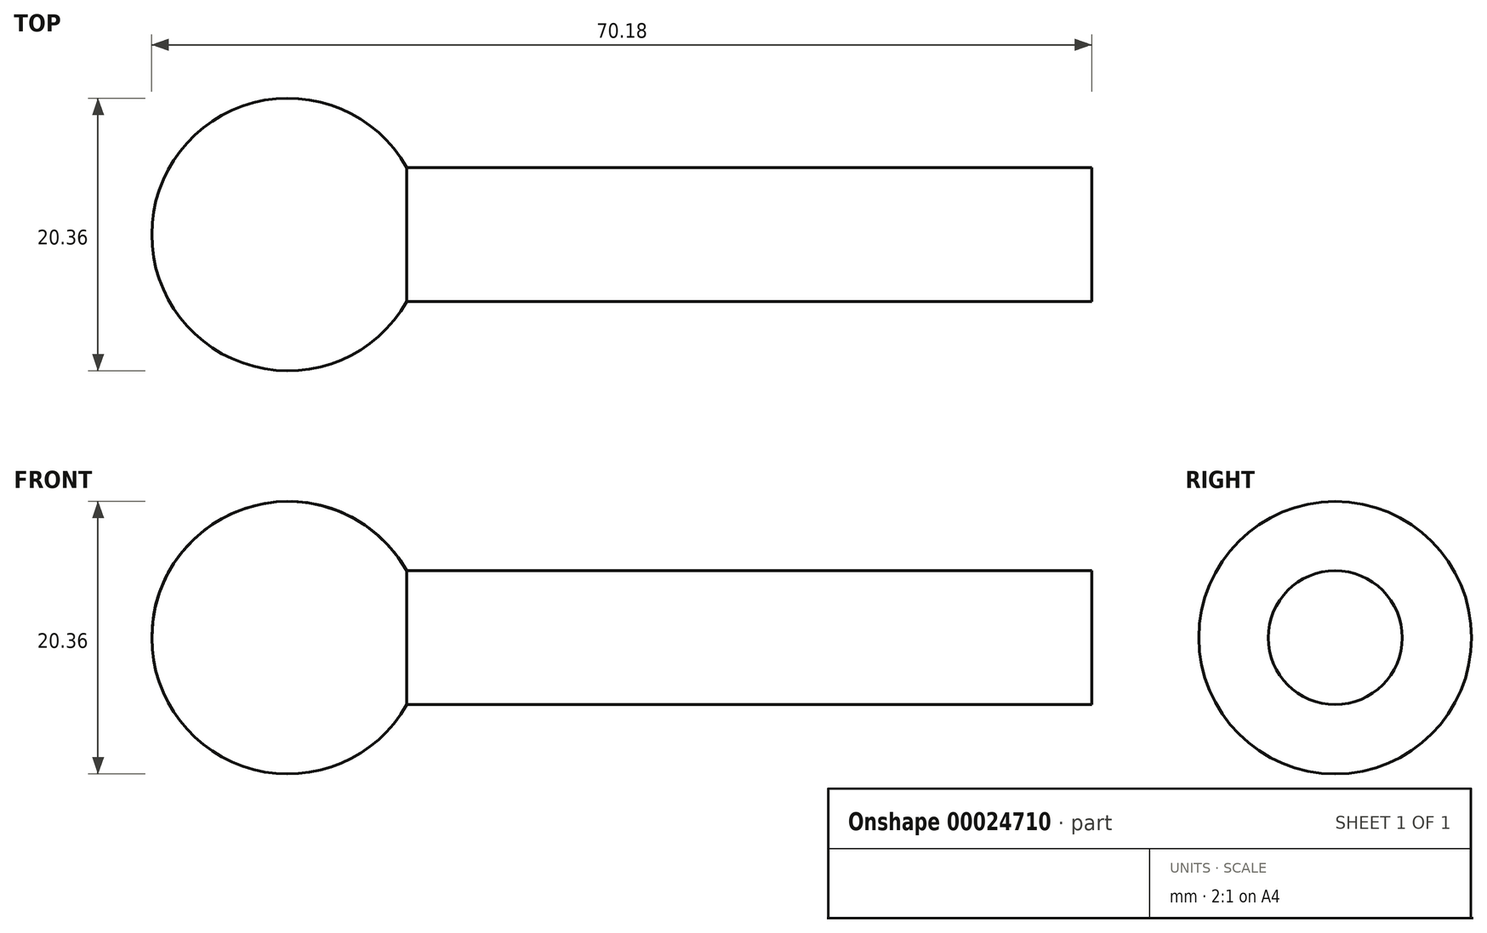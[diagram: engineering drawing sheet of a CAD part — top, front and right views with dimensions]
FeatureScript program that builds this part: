
annotation { "Feature Type Name" : "Feature", "Feature Type Description" : "" }
export const myFeature = defineFeature(function(context is Context, id is Id, definition is map)
    precondition{}
    {
        {
            var Q0;
            Q0=qCreatedBy(makeId("Front.planeOp"),FACE);
            var sketch = newSketch(context, id + "F0", { "sketchPlane" : qUnion([Q0])});
            skLineSegment(sketch, "E0", {"start": v(0, 0) * mm, "end": v(60, 0) * mm});
            skLineSegment(sketch, "E1", {"start": v(60, 0) * mm, "end": v(60, 5) * mm});
            skLineSegment(sketch, "E2", {"start": v(60, 5) * mm, "end": v(8.86, 5) * mm});
            skArc(sketch, "E3", {"start": v(8.86, 5) * mm, "mid": v(-2.58, 9.84) * mm, "end": v(-10.18, 0) * mm});
            skLineSegment(sketch, "E4", {"start": v(0, 0) * mm, "end": v(-10.18, 0) * mm});
            skPoint(sketch, "E5.orphan", {"position": v(0, 5) * mm});
            skSolve(sketch);
        }
        {
            var Q0;
            Q0=makeQuery(id+"F0.imprint","IMPRINT",FACE,{"disambiguationData":[TD([[makeQuery(id+"F0.imprint","IMPRINT",EDGE,{"derivedFrom":sQuery(id+"F0.wireOp",EDGE,"E0")}),1.0]])]});
            var Q1;
            Q1=sQuery(id+"F0.wireOp",EDGE,"E0");
            revolve(context, id + "F1", {"entities" : qUnion([Q0]), "axis" : qUnion([Q1]), "revolveType" : RevolveType.FULL});
        }
    });
